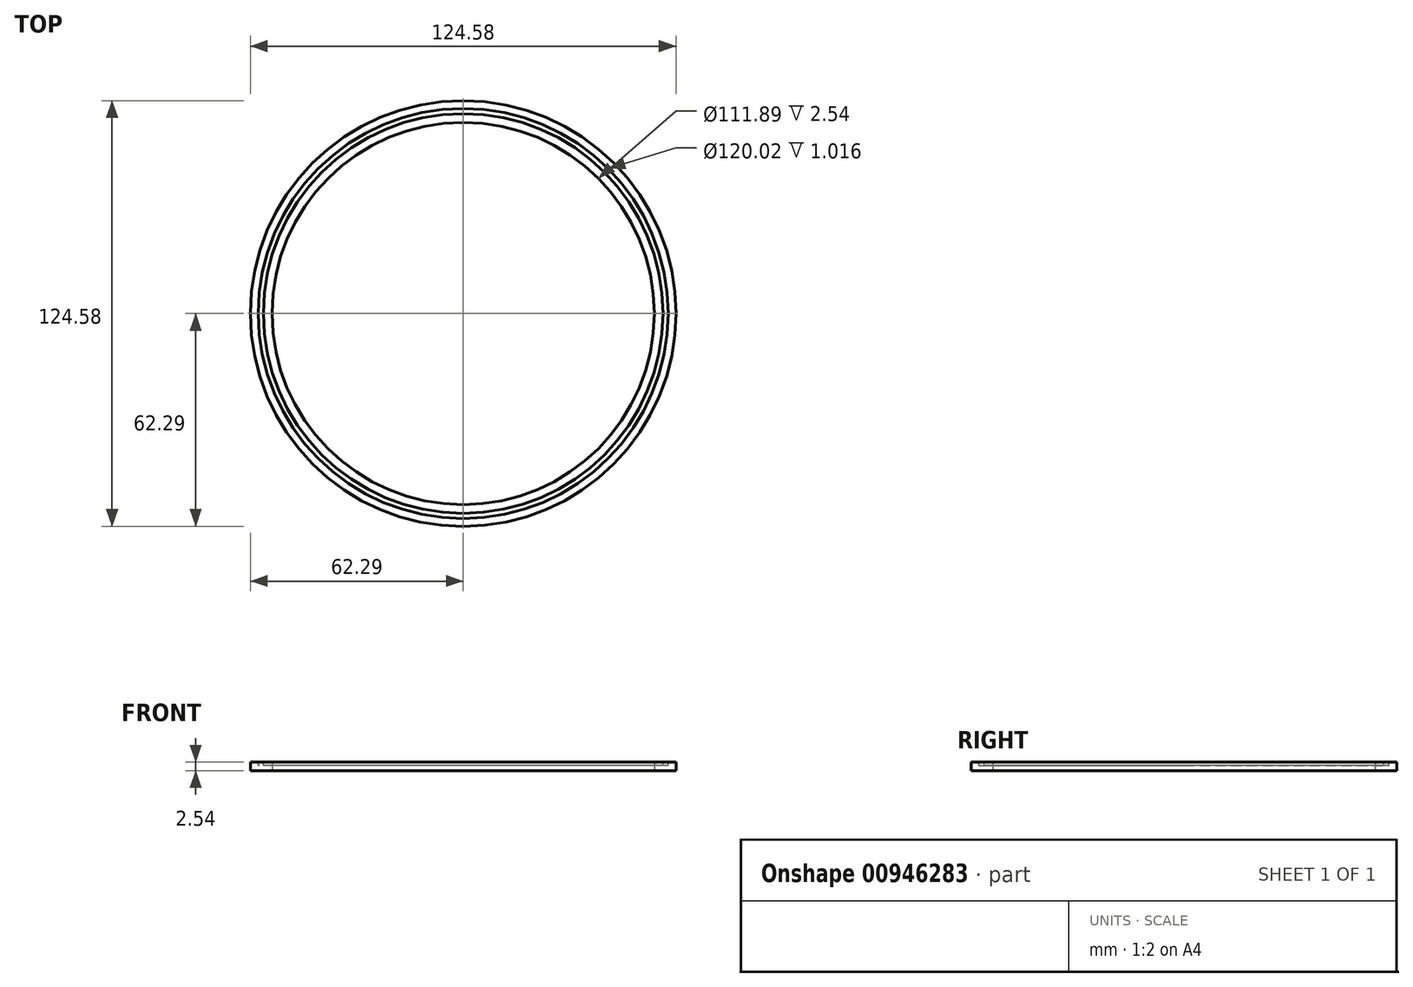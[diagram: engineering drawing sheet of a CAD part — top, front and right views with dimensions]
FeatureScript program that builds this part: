
annotation { "Feature Type Name" : "Feature", "Feature Type Description" : "" }
export const myFeature = defineFeature(function(context is Context, id is Id, definition is map)
    precondition{}
    {
        {
            var Q0;
            Q0=qCreatedBy(makeId("Top.planeOp"),FACE);
            var sketch = newSketch(context, id + "F0", { "sketchPlane" : qUnion([Q0])});
            skCircle(sketch, "E0", {"center": v(0, 0) * mm, "radius": 55.94 * mm});
            skCircle(sketch, "E1", {"center": v(0, 0) * mm, "radius": 62.3 * mm});
            skSolve(sketch);
        }
        {
            var Q0;
            Q0=qSketchRegion(id+"F0",true);
            extrude(context, id + "F1", {"entities" : qUnion([Q0]), "depth" : 2.54 * mm, "offsetDistance" : 25.4 * mm});
        }
        {
            var Q0;
            Q0=makeQuery(id+"F1.opExtrude","CAP_FACE",FACE,{"disambiguationData":[OSD([sQuery(id+"F0.wireOp",EDGE,"E0"),sQuery(id+"F0.wireOp",EDGE,"E1")])],"isStart":false});
            var sketch = newSketch(context, id + "F2", { "sketchPlane" : qUnion([Q0])});
            skCircle(sketch, "E2", {"center": v(0, 0) * mm, "radius": 60 * mm});
            skCircle(sketch, "E3", {"center": v(0, 0) * mm, "radius": 58.48 * mm});
            skSolve(sketch);
        }
        {
            var Q0;
            Q0 = qSketchRegion(id + "F2", true);
            extrude(context, id + "F3", {"entities" : qUnion([Q0]), "operationType" : NewBodyOperationType.REMOVE, "oppositeDirection" : true, "depth" : 1.02 * mm, "offsetDistance" : 25.4 * mm});
        }
    });
